# Revit family: 02-75-006 DN450-500 Reduced Bore
name_source: partatom
category: Pipe Accessories
units: mm (PartAtom-declared; Revit-internal decimal feet)

## family parameters
Always vertical = Yes
Cut with Voids When Loaded = No
Part Type = Valve - Breaks Into
Round Connector Dimension = Use Diameter
Shared = No
Work Plane-Based = No

## types (4) — shared parameters
1 = 1 mm  [stored 0.00328084 ft]
5 = 5 mm  [stored 0.0164042 ft]
Body_T = 14 mm  [stored 0.0459318 ft]
DN450_PN10 = 02-450-75-50464
DN450_PN16 = 02-450-75-51464
DN500_PN10 = 02-500-75-50464
DN500_PN16 = 02-500-75-51464
Description_ = AVK GATE VALVE, FLANGED, PN10/16
F = 14 mm  [stored 0.0459318 ft]
F0 = 32 mm  [stored 0.104987 ft]
F1 = 15 mm  [stored 0.0492126 ft]
F11 = 37 mm  [stored 0.121391 ft]
F2 = 38 mm  [stored 0.124672 ft]
F22 = 55 mm  [stored 0.180446 ft]
H = 1016 mm
H1 = 856 mm
Raised_dis = 4 mm  [stored 0.0131234 ft]
Search_table = 02-75-006 DN450-500 Reduced Bore
Stem_R = 41 mm
Stem_cap_H = 115 mm  [stored 0.377297 ft]
Stem_cap_dia = 75 mm  [stored 0.246063 ft]
URL_product_pages = https://www.avkvalves.com
zero-valued in all types: Default Elevation

## per-type parameters (varying)
- DN450_PN10: Body_FL_L=300 mm; Body_FL_T=60 mm  [stored 0.19685 ft]; Body_FL_W=133 mm  [stored 0.436352 ft]; Body_H=530 mm; Body_L=250 mm; Body_R=42 mm  [stored 0.137795 ft]; Body_W=93 mm; Bonnet_L=240 mm; Bonnet_dim1=88 mm; Bonnet_dim2=53 mm  [stored 0.173885 ft]; Bore=225 mm; DN=450 mm; FL_R=73 mm; FL_T=26 mm; H3=1336 mm; H3-H=320 mm; L=650 mm; L/2=325 mm; Logo height=451 mm; Nut=45 mm  [stored 0.147638 ft]; Raised_Dia=265 mm; Reduced_dim=288 mm; Reduced_dim1=102 mm; Rib_H=138 mm; Rib_L=288 mm; Rib_T=9 mm; Rib_W=106 mm; Stand_Rib_W=160 mm; disk_T=117 mm
- DN450_PN16: Body_FL_L=300 mm; Body_FL_T=60 mm  [stored 0.19685 ft]; Body_FL_W=133 mm  [stored 0.436352 ft]; Body_H=530 mm; Body_L=250 mm; Body_R=42 mm  [stored 0.137795 ft]; Body_W=93 mm; Bonnet_L=240 mm; Bonnet_dim1=88 mm; Bonnet_dim2=53 mm  [stored 0.173885 ft]; Bore=225 mm; DN=450 mm; FL_R=73 mm; FL_T=30 mm  [stored 0.0984252 ft]; H3=1336 mm; H3-H=320 mm; L=650 mm; L/2=325 mm; Logo height=451 mm; Nut=45 mm  [stored 0.147638 ft]; Raised_Dia=274 mm; Reduced_dim=288 mm; Reduced_dim1=102 mm; Rib_H=138 mm; Rib_L=288 mm; Rib_T=11 mm; Rib_W=106 mm; Stand_Rib_W=160 mm; disk_T=117 mm
- DN500_PN10: Body_FL_L=310 mm; Body_FL_T=65 mm  [stored 0.213255 ft]; Body_FL_W=143 mm; Body_H=560 mm; Body_L=290 mm; Body_R=47 mm  [stored 0.154199 ft]; Body_W=105 mm  [stored 0.344488 ft]; Bonnet_L=242 mm; Bonnet_dim1=100 mm  [stored 0.328084 ft]; Bonnet_dim2=60 mm  [stored 0.19685 ft]; Bore=250 mm; DN=500 mm; FL_R=78 mm  [stored 0.255906 ft]; FL_T=27 mm  [stored 0.0885827 ft]; H3=1373 mm; H3-H=357 mm; L=700 mm; L/2=350 mm; Logo height=476 mm; Nut=51 mm; Raised_Dia=291 mm; Reduced_dim=321 mm; Reduced_dim1=116 mm; Rib_H=146 mm; Rib_L=334 mm; Rib_T=9 mm; Rib_W=121 mm; Stand_Rib_W=179 mm; disk_T=133 mm  [stored 0.436352 ft]
- DN500_PN16: Body_FL_L=310 mm; Body_FL_T=65 mm  [stored 0.213255 ft]; Body_FL_W=143 mm; Body_H=560 mm; Body_L=290 mm; Body_R=47 mm  [stored 0.154199 ft]; Body_W=105 mm  [stored 0.344488 ft]; Bonnet_L=242 mm; Bonnet_dim1=100 mm  [stored 0.328084 ft]; Bonnet_dim2=60 mm  [stored 0.19685 ft]; Bore=250 mm; DN=500 mm; FL_R=78 mm  [stored 0.255906 ft]; FL_T=32 mm  [stored 0.104987 ft]; H3=1373 mm; H3-H=357 mm; L=700 mm; L/2=350 mm; Logo height=476 mm; Nut=51 mm; Raised_Dia=305 mm; Reduced_dim=321 mm; Reduced_dim1=116 mm; Rib_H=146 mm; Rib_L=334 mm; Rib_T=11 mm; Rib_W=121 mm; Stand_Rib_W=179 mm; disk_T=133 mm  [stored 0.436352 ft]

note: [stored X ft] marks values corroborated as IEEE doubles in the binary element streams (Revit-internal decimal feet)

## geometry (parser evidence)
native form markers: Sweep x2
no freeform markers — native parametric forms only
